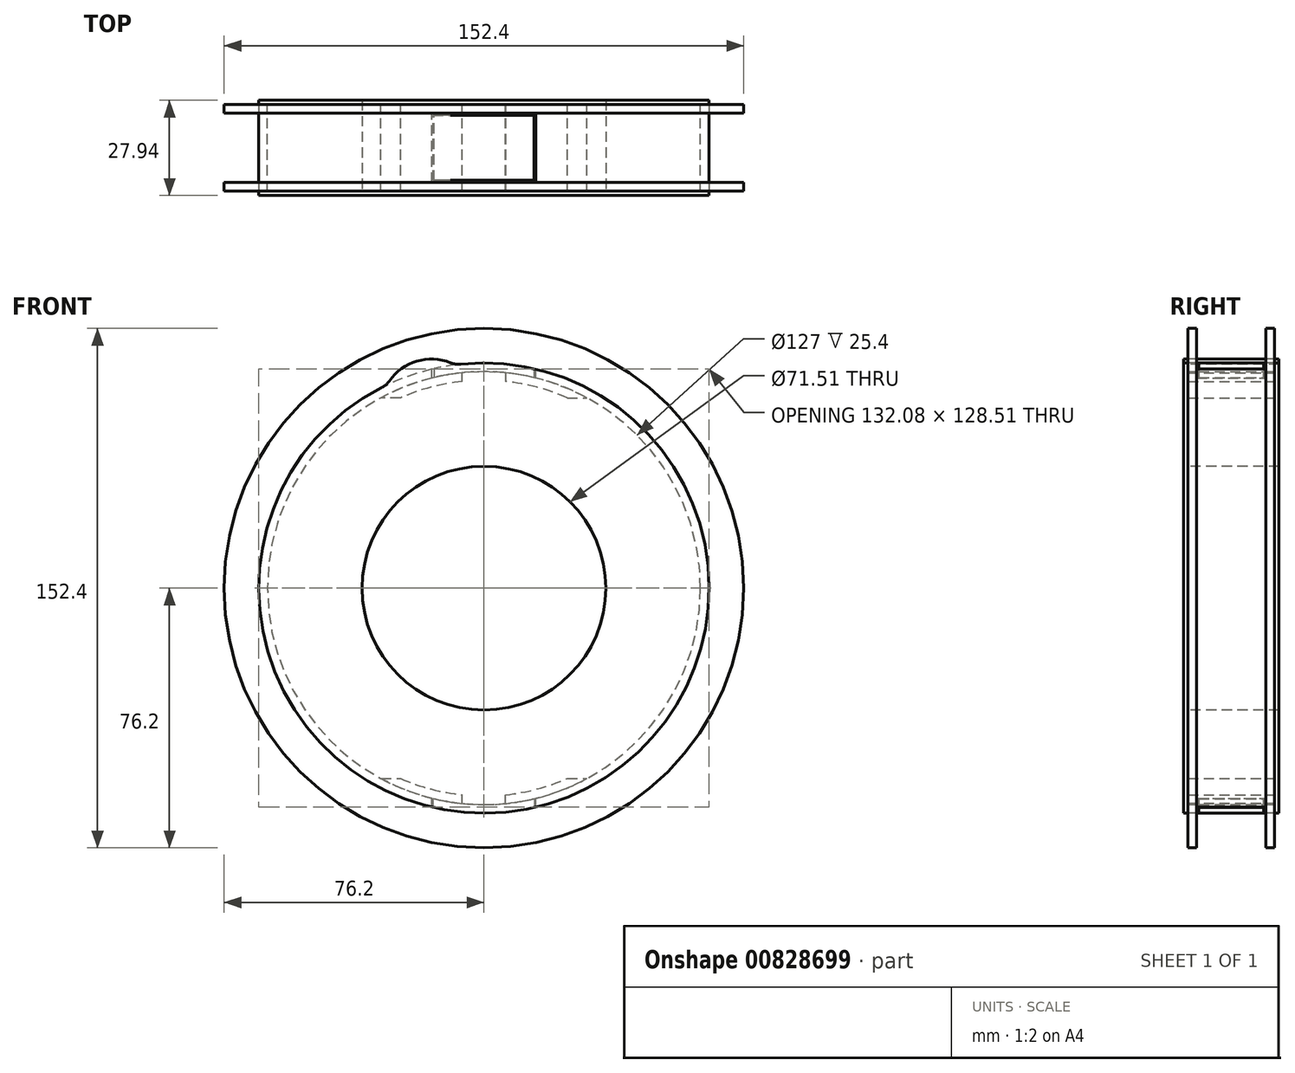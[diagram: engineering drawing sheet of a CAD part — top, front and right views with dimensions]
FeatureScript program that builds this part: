
annotation { "Feature Type Name" : "Feature", "Feature Type Description" : "" }
export const myFeature = defineFeature(function(context is Context, id is Id, definition is map)
    precondition{}
    {
        {
            var Q0;
            Q0=qCreatedBy(makeId("Front.planeOp"),FACE);
            var sketch = newSketch(context, id + "F0", { "sketchPlane" : qUnion([Q0])});
            skCircle(sketch, "E0", {"center": v(0, 0) * mm, "radius": 63.5 * mm});
            skCircle(sketch, "E1", {"center": v(0, 0) * mm, "radius": 76.2 * mm});
            skSolve(sketch);
        }
        {
            var Q0;
            Q0=qSketchRegion(id+"F0",true);
            extrude(context, id + "F1", {"entities" : qUnion([Q0]), "depth" : 25.4 * mm, "offsetDistance" : 25.4 * mm, "symmetric" : true});
        }
        {
            var Q0;
            Q0=qCreatedBy(makeId("Top.planeOp"),FACE);
            var sketch = newSketch(context, id + "F2", { "sketchPlane" : qUnion([Q0])});
            skLineSegment(sketch, "E2", {"start": v(-15.24, -10.16) * mm, "end": v(-15.24, 10.16) * mm});
            skLineSegment(sketch, "E3", {"start": v(15.24, -10.16) * mm, "end": v(15.24, 10.16) * mm});
            skLineSegment(sketch, "E4", {"start": v(15.24, -10.16) * mm, "end": v(-15.24, -10.16) * mm});
            skLineSegment(sketch, "E5", {"start": v(15.24, 10.16) * mm, "end": v(-15.24, 10.16) * mm});
            skLineSegment(sketch, "E6", {"start": v(0, 39.62) * mm, "end": v(0, -54.89) * mm});
            skLineSegment(sketch, "E7", {"start": v(22.27, 0) * mm, "end": v(-22.66, 0) * mm, "construction": true});
            skPoint(sketch, "E7.startSnap0", {"position": v(-15.24, 0) * mm});
            skSolve(sketch);
        }
        {
            var Q0;
            Q0=makeQuery(id+"F1.opExtrude","SWEPT_FACE",FACE,{"disambiguationData":[OSD([sQuery(id+"F0.wireOp",EDGE,"E1")])]});
            shell(context, id + "F3", {"entities" : qUnion([Q0]), "thickness" : 2.54 * mm});
        }
        {
            var Q0;
            Q0=qSketchRegion(id+"F2",true);
            extrude(context, id + "F4", {"entities" : qUnion([Q0]), "operationType" : NewBodyOperationType.REMOVE, "oppositeDirection" : true, "depth" : 132.08 * mm, "offsetDistance" : 25.4 * mm, "symmetric" : true});
        }
        {
            var Q0;
            Q0=qCreatedBy(makeId("Front.planeOp"),FACE);
            var sketch = newSketch(context, id + "F5", { "sketchPlane" : qUnion([Q0])});
            skArc(sketch, "E8", {"start": v(14.74, 61.76) * mm, "mid": v(0.03, 63.5) * mm, "end": v(-14.68, 61.78) * mm});
            skArc(sketch, "E9", {"start": v(-14.96, -64.32) * mm, "mid": v(-0.07, -66.04) * mm, "end": v(14.83, -64.35) * mm});
            skLineSegment(sketch, "E10", {"start": v(-14.68, 64.39) * mm, "end": v(-14.68, 61.78) * mm});
            skLineSegment(sketch, "E11", {"start": v(14.74, 64.37) * mm, "end": v(14.74, 61.76) * mm});
            skLineSegment(sketch, "E12", {"start": v(14.83, -61.74) * mm, "end": v(14.83, -64.35) * mm});
            skLineSegment(sketch, "E13", {"start": v(-14.96, -64.32) * mm, "end": v(-14.96, -61.71) * mm});
            skArc(sketch, "E14.trimOffspring", {"start": v(-14.96, -61.71) * mm, "mid": v(-0.07, -63.5) * mm, "end": v(14.83, -61.74) * mm});
            skArc(sketch, "E15.trimOffspring", {"start": v(14.74, 64.37) * mm, "mid": v(0.03, 66.04) * mm, "end": v(-14.68, 64.39) * mm});
            skSolve(sketch);
        }
        {
            var Q0;
            Q0=qSketchRegion(id+"F5",true);
            extrude(context, id + "F6", {"entities" : qUnion([Q0]), "depth" : 19.05 * mm, "offsetDistance" : 25.4 * mm, "symmetric" : true});
        }
        {
            var Q0;
            Q0=qCreatedBy(makeId("Front.planeOp"),FACE);
            var sketch = newSketch(context, id + "F7", { "sketchPlane" : qUnion([Q0])});
            skArc(sketch, "E16", {"start": v(-24.43, -55.85) * mm, "mid": v(-15.58, -58.94) * mm, "end": v(-6.35, -60.63) * mm});
            skLineSegment(sketch, "E17", {"start": v(-6.35, 60.63) * mm, "end": v(-6.35, 63.17) * mm});
            skLineSegment(sketch, "E18", {"start": v(6.35, 63.17) * mm, "end": v(6.35, 60.63) * mm});
            skLineSegment(sketch, "E19", {"start": v(29.54, 56.4) * mm, "end": v(23.14, 56.4) * mm});
            skLineSegment(sketch, "E20.trimOffspring", {"start": v(-23.14, 56.4) * mm, "end": v(-29.35, 56.4) * mm});
            skLineSegment(sketch, "E21", {"start": v(-6.35, -63.17) * mm, "end": v(-6.35, -60.63) * mm});
            skLineSegment(sketch, "E22", {"start": v(6.35, -63.17) * mm, "end": v(6.35, -60.63) * mm});
            skLineSegment(sketch, "E23", {"start": v(-30.22, -55.85) * mm, "end": v(-24.43, -55.85) * mm});
            skArc(sketch, "E24", {"start": v(-30.22, -55.85) * mm, "mid": v(-18.62, -60.7) * mm, "end": v(-6.29, -63.19) * mm});
            skArc(sketch, "E25.trimOffspring", {"start": v(23.14, 56.4) * mm, "mid": v(14.9, 59.11) * mm, "end": v(6.35, 60.63) * mm});
            skArc(sketch, "E26.trimOffspring", {"start": v(6.35, -60.63) * mm, "mid": v(15.58, -58.94) * mm, "end": v(24.43, -55.85) * mm});
            skArc(sketch, "E27.trimOffspring", {"start": v(-6.35, 60.63) * mm, "mid": v(-14.9, 59.11) * mm, "end": v(-23.14, 56.4) * mm});
            skArc(sketch, "E28.trimOffspring", {"start": v(-6.35, 63.18) * mm, "mid": v(-18.09, 60.87) * mm, "end": v(-29.18, 56.4) * mm});
            skLineSegment(sketch, "E29", {"start": v(24.43, -55.85) * mm, "end": v(30.22, -55.85) * mm});
            skArc(sketch, "E30.trimOffspring", {"start": v(29.18, 56.4) * mm, "mid": v(18.09, 60.87) * mm, "end": v(6.35, 63.18) * mm});
            skArc(sketch, "E31.trimOffspring", {"start": v(6.4, -63.18) * mm, "mid": v(18.67, -60.7) * mm, "end": v(30.22, -55.85) * mm});
            skLineSegment(sketch, "E32.trimOffspring", {"start": v(6.35, -63.13) * mm, "end": v(6.4, -63.18) * mm});
            skLineSegment(sketch, "E33.MirrorCS", {"start": v(-6.35, -63.13) * mm, "end": v(-6.4, -63.18) * mm});
            skArc(sketch, "E34.MirrorCS", {"start": v(-6.35, -60.63) * mm, "mid": v(-15.58, -58.94) * mm, "end": v(-24.43, -55.85) * mm});
            skLineSegment(sketch, "E35.MirrorCS", {"start": v(-24.43, -55.85) * mm, "end": v(-30.22, -55.85) * mm});
            skArc(sketch, "E36.MirrorCS", {"start": v(-6.4, -63.18) * mm, "mid": v(-18.67, -60.7) * mm, "end": v(-30.22, -55.85) * mm});
            skLineSegment(sketch, "E37.MirrorCS", {"start": v(30.22, -55.85) * mm, "end": v(24.43, -55.85) * mm});
            skArc(sketch, "E38.MirrorCS", {"start": v(30.22, -55.85) * mm, "mid": v(18.62, -60.7) * mm, "end": v(6.29, -63.19) * mm});
            skArc(sketch, "E39.MirrorCS", {"start": v(24.43, -55.85) * mm, "mid": v(15.58, -58.94) * mm, "end": v(6.35, -60.63) * mm});
            skLineSegment(sketch, "E40.MirrorCS", {"start": v(6.35, 63.13) * mm, "end": v(6.4, 63.18) * mm});
            skLineSegment(sketch, "E41.MirrorCS", {"start": v(-6.35, 63.13) * mm, "end": v(-6.4, 63.18) * mm});
            skLineSegment(sketch, "E42.MirrorCS", {"start": v(-6.35, 63.17) * mm, "end": v(-6.35, 60.63) * mm});
            skLineSegment(sketch, "E43.MirrorCS", {"start": v(24.43, 55.85) * mm, "end": v(30.22, 55.85) * mm});
            skLineSegment(sketch, "E44.MirrorCS", {"start": v(-24.43, 55.85) * mm, "end": v(-30.22, 55.85) * mm});
            skArc(sketch, "E45.MirrorCS", {"start": v(6.4, 63.18) * mm, "mid": v(18.67, 60.7) * mm, "end": v(30.22, 55.85) * mm});
            skLineSegment(sketch, "E46.MirrorCS", {"start": v(-30.22, 55.85) * mm, "end": v(-24.43, 55.85) * mm});
            skArc(sketch, "E47.MirrorCS", {"start": v(-6.35, 60.63) * mm, "mid": v(-15.58, 58.94) * mm, "end": v(-24.43, 55.85) * mm});
            skArc(sketch, "E48.MirrorCS", {"start": v(-6.4, 63.18) * mm, "mid": v(-18.67, 60.7) * mm, "end": v(-30.22, 55.85) * mm});
            skArc(sketch, "E49.MirrorCS", {"start": v(6.35, 60.63) * mm, "mid": v(15.58, 58.94) * mm, "end": v(24.43, 55.85) * mm});
            skLineSegment(sketch, "E50.MirrorCS", {"start": v(30.22, 55.85) * mm, "end": v(24.43, 55.85) * mm});
            skArc(sketch, "E51.MirrorCS", {"start": v(30.22, 55.85) * mm, "mid": v(18.62, 60.7) * mm, "end": v(6.29, 63.19) * mm});
            skArc(sketch, "E52.MirrorCS", {"start": v(-24.43, 55.85) * mm, "mid": v(-15.58, 58.94) * mm, "end": v(-6.35, 60.63) * mm});
            skArc(sketch, "E53.MirrorCS", {"start": v(24.43, 55.85) * mm, "mid": v(15.58, 58.94) * mm, "end": v(6.35, 60.63) * mm});
            skArc(sketch, "E54.MirrorCS", {"start": v(-30.22, 55.85) * mm, "mid": v(-18.62, 60.7) * mm, "end": v(-6.29, 63.19) * mm});
            skSolve(sketch);
        }
        {
            var Q0;
            Q0=qSketchRegion(id+"F7",true);
            extrude(context, id + "F8", {"entities" : qUnion([Q0]), "depth" : 25.4 * mm, "offsetDistance" : 25.4 * mm, "symmetric" : true});
        }
        {
            var Q0;
            Q0=qCreatedBy(makeId("Front.planeOp"),FACE);
            var sketch = newSketch(context, id + "F9", { "sketchPlane" : qUnion([Q0])});
            skArc(sketch, "E55", {"start": v(-30.06, 58.8) * mm, "mid": v(18.73, -63.33) * mm, "end": v(-6.75, 65.7) * mm});
            skArc(sketch, "E56", {"start": v(-9.77, 66.12) * mm, "mid": v(-19.7, 66.59) * mm, "end": v(-27.76, 60.8) * mm});
            skPoint(sketch, "E57.visualSharp", {"position": v(-28.55, 59.55) * mm});
            skArc(sketch, "E57.filletArc", {"start": v(-30.06, 58.8) * mm, "mid": v(-28.8, 59.66) * mm, "end": v(-27.76, 60.8) * mm});
            skPoint(sketch, "E58.visualSharp", {"position": v(-8.42, 65.5) * mm});
            skArc(sketch, "E58.filletArc", {"start": v(-9.77, 66.12) * mm, "mid": v(-8.29, 65.72) * mm, "end": v(-6.75, 65.7) * mm});
            skCircle(sketch, "E59", {"center": v(0, 0) * mm, "radius": 35.75 * mm});
            skSolve(sketch);
        }
        {
            var Q0;
            Q0 = qSketchRegion(id + "F9", true);
            var Q1;
            Q1=sQuery(id+"F9.wireOp",EDGE,"E55");
            var Q2;
            Q2=sQuery(id+"F9.wireOp",EDGE,"E57.filletArc");
            var Q3;
            Q3=sQuery(id+"F9.wireOp",EDGE,"E56");
            var Q4;
            Q4=sQuery(id+"F9.wireOp",EDGE,"E58.filletArc");
            extrude(context, id + "F10", {"entities" : qUnion([Q0]), "surfaceEntities" : qUnion([Q1, Q2, Q3, Q4]), "oppositeDirection" : true, "depth" : 27.94 * mm, "offsetDistance" : 25.4 * mm, "symmetric" : true});
        }
    });
